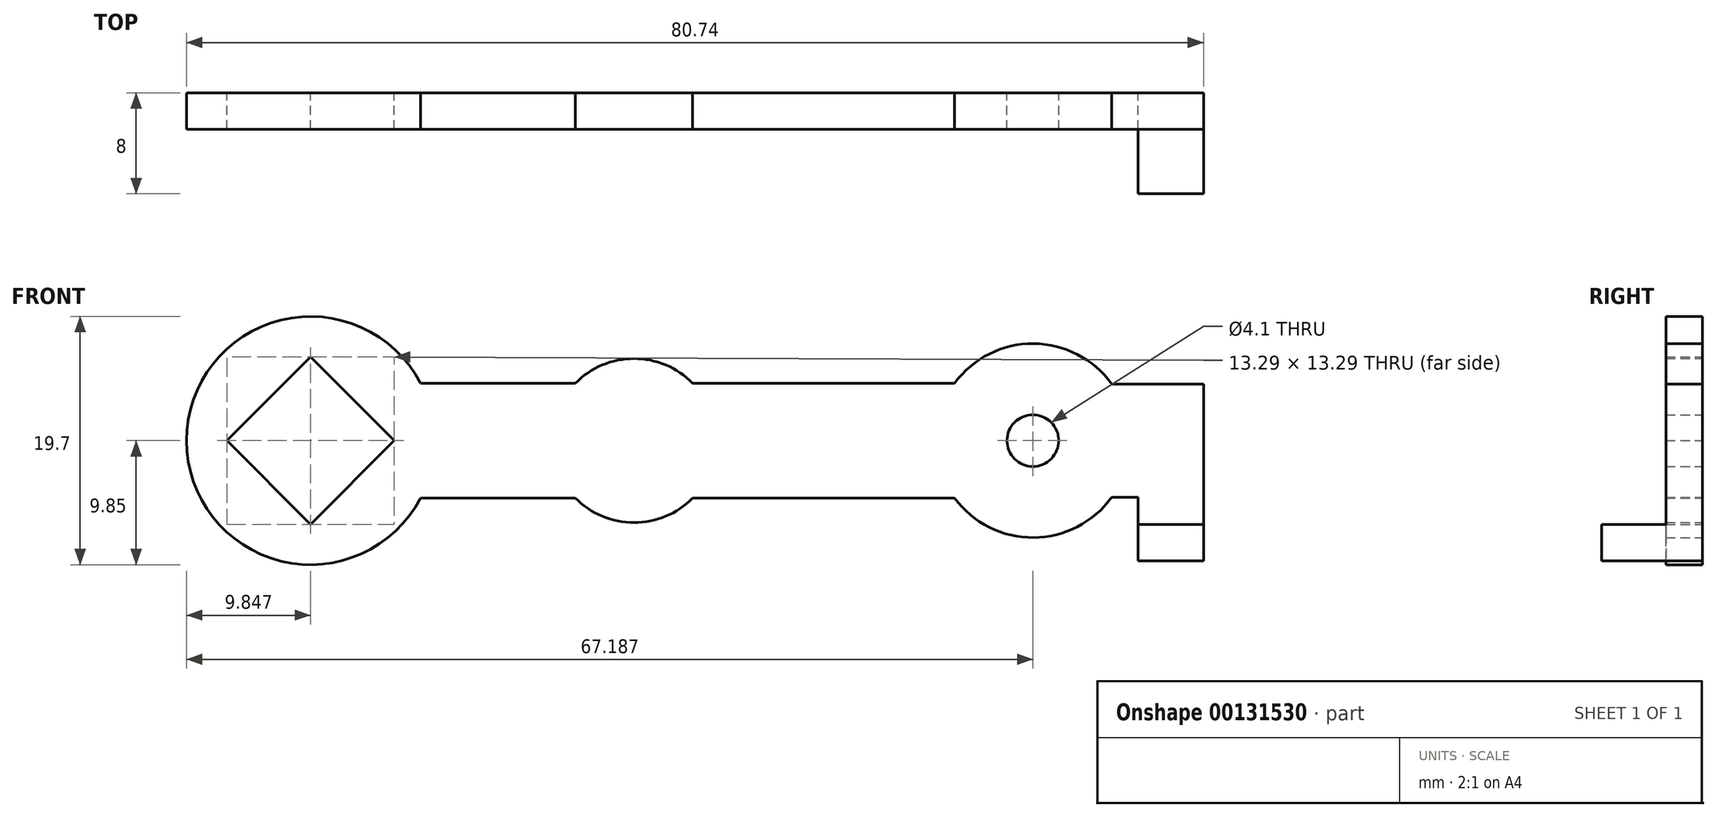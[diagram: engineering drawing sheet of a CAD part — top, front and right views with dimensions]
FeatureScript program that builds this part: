
annotation { "Feature Type Name" : "Feature", "Feature Type Description" : "" }
export const myFeature = defineFeature(function(context is Context, id is Id, definition is map)
    precondition{}
    {
        {
            var Q0;
            Q0=qCreatedBy(makeId("Front.planeOp"),FACE);
            var sketch = newSketch(context, id + "F0", { "sketchPlane" : qUnion([Q0])});
            skArc(sketch, "E0", {"start": v(4.65, 4.56) * mm, "mid": v(0, 6.5) * mm, "end": v(-4.65, 4.56) * mm});
            skCircle(sketch, "E1", {"center": v(31.66, 0) * mm, "radius": 2.05 * mm});
            skArc(sketch, "E2", {"start": v(25.45, -4.56) * mm, "mid": v(31.7, -7.7) * mm, "end": v(37.9, -4.5) * mm});
            skArc(sketch, "E3", {"start": v(-16.95, 4.56) * mm, "mid": v(-35.53, 0) * mm, "end": v(-16.95, -4.56) * mm});
            skLineSegment(sketch, "E4", {"start": v(-4.65, 4.56) * mm, "end": v(-16.95, 4.56) * mm});
            skLineSegment(sketch, "E5", {"start": v(4.65, 4.56) * mm, "end": v(25.45, 4.56) * mm});
            skLineSegment(sketch, "E6", {"start": v(-4.65, -4.56) * mm, "end": v(-16.95, -4.56) * mm});
            skLineSegment(sketch, "E7", {"start": v(4.65, -4.56) * mm, "end": v(25.45, -4.56) * mm});
            skArc(sketch, "E8.trimOffspring", {"start": v(-4.65, -4.56) * mm, "mid": v(0, -6.5) * mm, "end": v(4.65, -4.56) * mm});
            skLineSegment(sketch, "E9", {"start": v(-25.68, 6.65) * mm, "end": v(-19.04, 0) * mm});
            skLineSegment(sketch, "E10", {"start": v(-32.33, 0) * mm, "end": v(-25.68, 6.65) * mm});
            skLineSegment(sketch, "E11", {"start": v(-25.68, -6.65) * mm, "end": v(-19.04, 0) * mm});
            skLineSegment(sketch, "E12", {"start": v(-25.68, -6.65) * mm, "end": v(-32.33, 0) * mm});
            skLineSegment(sketch, "E13", {"start": v(45.2, 4.5) * mm, "end": v(45.2, -9.55) * mm});
            skLineSegment(sketch, "E14", {"start": v(45.2, -9.55) * mm, "end": v(40, -9.55) * mm});
            skArc(sketch, "E15.trimOffspring", {"start": v(37.9, 4.5) * mm, "mid": v(31.7, 7.7) * mm, "end": v(25.45, 4.56) * mm});
            skLineSegment(sketch, "E16", {"start": v(45.2, -6.65) * mm, "end": v(40, -6.65) * mm});
            skLineSegment(sketch, "E17", {"start": v(33.7, 0) * mm, "end": v(37.9, 0) * mm});
            skLineSegment(sketch, "E18", {"start": v(37.9, 0) * mm, "end": v(37.9, -4.5) * mm});
            skLineSegment(sketch, "E19", {"start": v(45.2, 4.5) * mm, "end": v(37.9, 4.5) * mm});
            skLineSegment(sketch, "E20", {"start": v(37.9, 0) * mm, "end": v(37.9, 4.5) * mm});
            skLineSegment(sketch, "E21", {"start": v(37.9, -4.5) * mm, "end": v(45.2, -4.5) * mm});
            skLineSegment(sketch, "E22", {"start": v(40, -9.55) * mm, "end": v(40, -4.5) * mm});
            skSolve(sketch);
        }
        {
            var Q0;
            Q0=makeQuery(id+"F0.imprint","IMPRINT",FACE,{"disambiguationData":[TD([[makeQuery(id+"F0.imprint","IMPRINT",EDGE,{"derivedFrom":sQuery(id+"F0.wireOp",EDGE,"E0")}),1.0]])]});
            var Q1;
            {var subQ1=sQuery(id+"F0.wireOp",EDGE,"E18");Q1=makeQuery(id+"F0.imprint","IMPRINT",FACE,{"disambiguationData":[TD([[makeQuery(id+"F0.imprint","IMPRINT",EDGE,{"derivedFrom":subQ1}),1.0]])]});}
            var Q2;
            {var subQ0=sQuery(id+"F0.wireOp",EDGE,"E16");Q2=makeQuery(id+"F0.imprint","IMPRINT",FACE,{"disambiguationData":[TD([[makeQuery(id+"F0.imprint","IMPRINT",EDGE,{"derivedFrom":subQ0}),-1.0]])]});}
            extrude(context, id + "F1", {"entities" : qUnion([Q0, Q1, Q2]), "depth" : 2.9 * mm});
        }
        {
            var Q0;
            {var subQ0=sQuery(id+"F0.wireOp",EDGE,"E14");Q0=makeQuery(id+"F0.imprint","IMPRINT",FACE,{"disambiguationData":[TD([[makeQuery(id+"F0.imprint","IMPRINT",EDGE,{"derivedFrom":subQ0}),-1.0]])]});}
            extrude(context, id + "F2", {"entities" : qUnion([Q0]), "operationType" : NewBodyOperationType.ADD, "depth" : 8 * mm});
        }
    });
